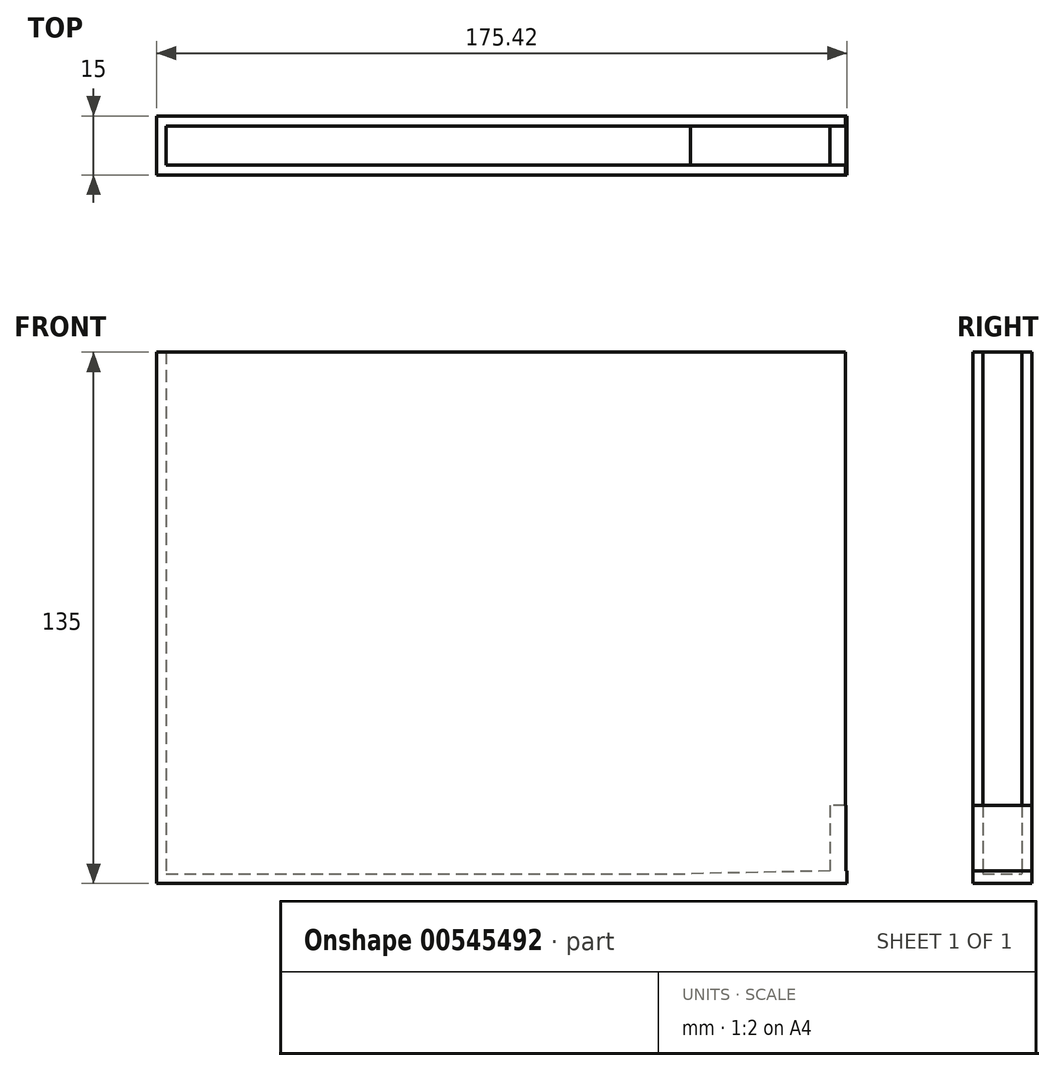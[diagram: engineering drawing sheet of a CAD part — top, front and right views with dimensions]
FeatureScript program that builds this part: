
annotation { "Feature Type Name" : "Feature", "Feature Type Description" : "" }
export const myFeature = defineFeature(function(context is Context, id is Id, definition is map)
    precondition{}
    {
        {
            var Q0;
            Q0=qCreatedBy(makeId("Front.planeOp"),FACE);
            var sketch = newSketch(context, id + "F0", { "sketchPlane" : qUnion([Q0])});
            skLineSegment(sketch, "E0.bottom", {"start": v(0, 0) * mm, "end": v(175, 0) * mm});
            skLineSegment(sketch, "E0.top", {"start": v(0, 135) * mm, "end": v(175, 135) * mm});
            skLineSegment(sketch, "E0.left", {"start": v(175, 135) * mm, "end": v(175, 0) * mm});
            skLineSegment(sketch, "E0.right", {"start": v(0, 135) * mm, "end": v(0, 0) * mm});
            skSolve(sketch);
        }
        {
            var Q0;
            Q0=makeQuery(id+"F0.imprint","IMPRINT",FACE,{"disambiguationData":[TD([[makeQuery(id+"F0.imprint","IMPRINT",EDGE,{"derivedFrom":sQuery(id+"F0.wireOp",EDGE,"E0.bottom")}),1.0]])]});
            extrude(context, id + "F1", {"entities" : qUnion([Q0]), "depth" : 15 * mm, "offsetDistance" : 25 * mm});
        }
        {
            var Q0;
            Q0=makeQuery(id+"F1.opExtrude","SWEPT_FACE",FACE,{"disambiguationData":[OSD([sQuery(id+"F0.wireOp",EDGE,"E0.top")])]});
            var Q1;
            Q1=makeQuery(id+"F1.opExtrude","SWEPT_FACE",FACE,{"disambiguationData":[OSD([sQuery(id+"F0.wireOp",EDGE,"E0.left")])]});
            shell(context, id + "F2", {"entities" : qUnion([Q0, Q1]), "thickness" : 2.5 * mm});
        }
        {
            var Q0;
            Q0=qCreatedBy(makeId("Front.planeOp"),FACE);
            var sketch = newSketch(context, id + "F3", { "sketchPlane" : qUnion([Q0])});
            skLineSegment(sketch, "E1", {"start": v(0, 0) * mm, "end": v(175.36, 3.23) * mm});
            skLineSegment(sketch, "E2", {"start": v(175.36, 3.23) * mm, "end": v(175.42, 0) * mm});
            skLineSegment(sketch, "E3", {"start": v(175.42, 0) * mm, "end": v(0, 0) * mm});
            skSolve(sketch);
        }
        {
            var Q0;
            Q0=qSketchRegion(id+"F3",true);
            extrude(context, id + "F4", {"entities" : qUnion([Q0]), "depth" : 15 * mm, "offsetDistance" : 25 * mm});
        }
        {
            var Q0;
            Q0=makeQuery(id+"F0.imprint","IMPRINT",FACE,{"disambiguationData":[TD([[makeQuery(id+"F0.imprint","IMPRINT",EDGE,{"derivedFrom":sQuery(id+"F0.wireOp",EDGE,"E0.bottom")}),1.0]])]});
            var sketch = newSketch(context, id + "F5", { "sketchPlane" : qUnion([Q0])});
            skLineSegment(sketch, "E4.bottom", {"start": v(171.16, 0) * mm, "end": v(175.2, 0) * mm});
            skLineSegment(sketch, "E4.top", {"start": v(171.16, 19.82) * mm, "end": v(175.2, 19.82) * mm});
            skLineSegment(sketch, "E4.left", {"start": v(171.16, 0) * mm, "end": v(171.16, 19.82) * mm});
            skLineSegment(sketch, "E4.right", {"start": v(175.2, 0) * mm, "end": v(175.2, 19.82) * mm});
            skLineSegment(sketch, "E5.left", {"start": v(171.16, 19.82) * mm, "end": v(171.16, 19.82) * mm});
            skLineSegment(sketch, "E6.right", {"start": v(171.16, 0) * mm, "end": v(171.16, 0) * mm});
            skSolve(sketch);
        }
        {
            var Q0;
            Q0=qSketchRegion(id+"F5",true);
            extrude(context, id + "F6", {"entities" : qUnion([Q0]), "operationType" : NewBodyOperationType.ADD, "depth" : 15 * mm, "offsetDistance" : 25 * mm});
        }
    });
